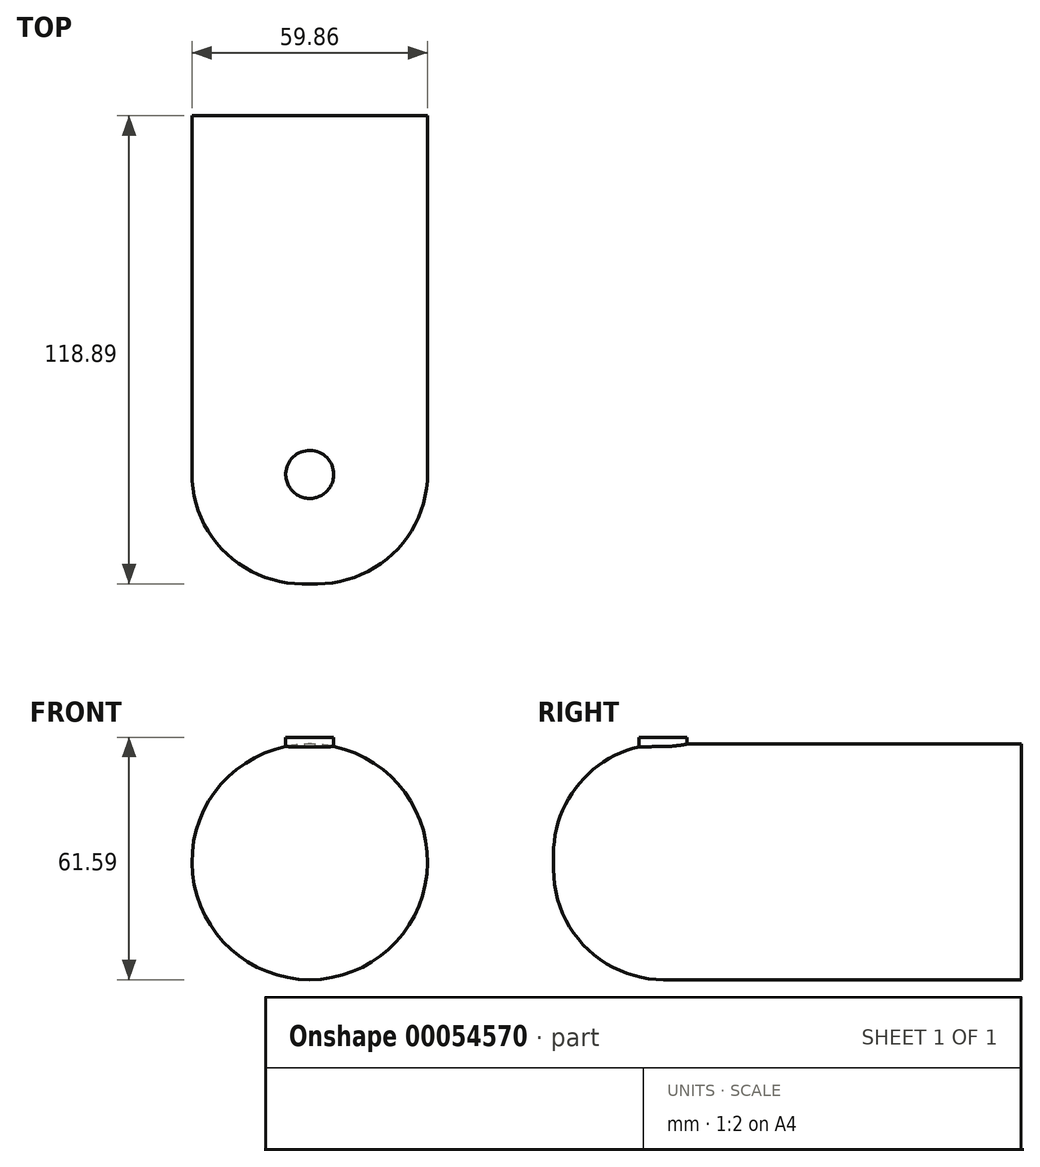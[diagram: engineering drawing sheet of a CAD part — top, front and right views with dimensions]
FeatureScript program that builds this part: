
annotation { "Feature Type Name" : "Feature", "Feature Type Description" : "" }
export const myFeature = defineFeature(function(context is Context, id is Id, definition is map)
    precondition{}
    {
        {
            var Q0;
            Q0=qCreatedBy(makeId("Front.planeOp"),FACE);
            var sketch = newSketch(context, id + "F0", { "sketchPlane" : qUnion([Q0])});
            skCircle(sketch, "E0", {"center": v(0, 0) * mm, "radius": 29.93 * mm});
            skSolve(sketch);
        }
        {
            var Q0;
            Q0 = qSketchRegion(id + "F0", true);
            var Q1;
            Q1 = qSketchRegion(id + "FvcO4RkDtDrDZsB_1", true);
            extrude(context, id + "F1", {"entities" : qUnion([Q0, Q1]), "depth" : 75.93 * mm});
        }
        {
            var Q0;
            Q0=makeQuery(id+"F1.opExtrude","CAP_EDGE",EDGE,{"disambiguationData":[OSD([sQuery(id+"F0.wireOp",EDGE,"E0")])],"isStart":false});
            fillet(context, id + "F2", {"entities" : qUnion([Q0]), "radius" : 27.98 * mm, "tangentPropagation" : true, "allowEdgeOverflow" : false});
        }
        {
            var Q0;
            Q0=makeQuery(id+"F1.opExtrude","CAP_FACE",FACE,{"disambiguationData":[OSD([sQuery(id+"F0.wireOp",EDGE,"E0")])],"isStart":true});
            extrude(context, id + "F3", {"entities" : qUnion([Q0]), "operationType" : NewBodyOperationType.ADD, "depth" : 42.96 * mm});
        }
        {
            var Q0;
            Q0=qCreatedBy(makeId("Top.planeOp"),FACE);
            var sketch = newSketch(context, id + "F4", { "sketchPlane" : qUnion([Q0])});
            skCircle(sketch, "E1", {"center": v(0, -48.15) * mm, "radius": 6.1 * mm});
            skSolve(sketch);
        }
        {
            var Q0;
            Q0 = qSketchRegion(id + "F4", true);
            extrude(context, id + "F5", {"entities" : qUnion([Q0]), "operationType" : NewBodyOperationType.ADD, "depth" : 31.66 * mm});
        }
        {
            var Q0;
            Q0=makeQuery(id+"F5.opExtrude","CAP_FACE",FACE,{"disambiguationData":[OSD([sQuery(id+"F4.wireOp",EDGE,"E1")])],"isStart":false});
            extrude(context, id + "F6", {"entities" : qUnion([Q0]), "operationType" : NewBodyOperationType.ADD, "oppositeDirection" : true, "depth" : 6.63 * mm});
        }
    });
